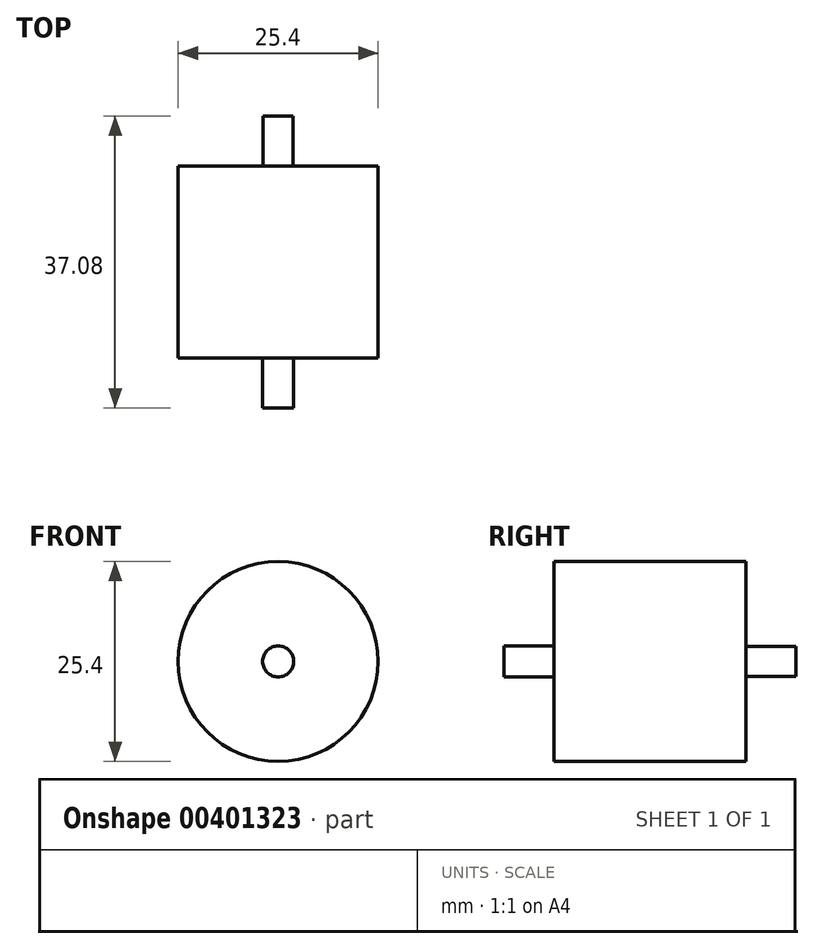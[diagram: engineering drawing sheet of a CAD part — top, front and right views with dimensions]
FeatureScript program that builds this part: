
annotation { "Feature Type Name" : "Feature", "Feature Type Description" : "" }
export const myFeature = defineFeature(function(context is Context, id is Id, definition is map)
    precondition{}
    {
        {
            var Q0;
            Q0=qCreatedBy(makeId("Front.planeOp"),FACE);
            var sketch = newSketch(context, id + "F0", { "sketchPlane" : qUnion([Q0])});
            skCircle(sketch, "E0", {"center": v(0, 0) * mm, "radius": 12.7 * mm});
            skSolve(sketch);
        }
        {
            var Q0;
            Q0=makeQuery(id+"F0.imprint","IMPRINT",FACE,{"disambiguationData":[TD([[makeQuery(id+"F0.imprint","IMPRINT",EDGE,{"derivedFrom":sQuery(id+"F0.wireOp",EDGE,"E0")}),1.0]])]});
            var Q1;
            Q1=sQuery(id+"F0.wireOp",EDGE,"E0");
            extrude(context, id + "F1", {"entities" : qUnion([Q0]), "surfaceEntities" : qUnion([Q1]), "depth" : 24.38 * mm});
        }
        {
            var Q0;
            Q0=qCreatedBy(makeId("Front.planeOp"),FACE);
            var sketch = newSketch(context, id + "F2", { "sketchPlane" : qUnion([Q0])});
            skCircle(sketch, "E1", {"center": v(0, 0) * mm, "radius": 1.97 * mm});
            skSolve(sketch);
        }
        {
            var Q0;
            Q0 = qSketchRegion(id + "F2", true);
            extrude(context, id + "F3", {"entities" : qUnion([Q0]), "operationType" : NewBodyOperationType.ADD, "depth" : 30.73 * mm});
        }
        {
            var Q0;
            Q0=qCreatedBy(makeId("Front.planeOp"),FACE);
            var sketch = newSketch(context, id + "F4", { "sketchPlane" : qUnion([Q0])});
            skCircle(sketch, "E2", {"center": v(0, 0) * mm, "radius": 1.9 * mm});
            skSolve(sketch);
        }
        {
            var Q0;
            Q0 = qSketchRegion(id + "F4", true);
            extrude(context, id + "F5", {"entities" : qUnion([Q0]), "operationType" : NewBodyOperationType.ADD, "oppositeDirection" : true, "depth" : 6.35 * mm});
        }
    });
